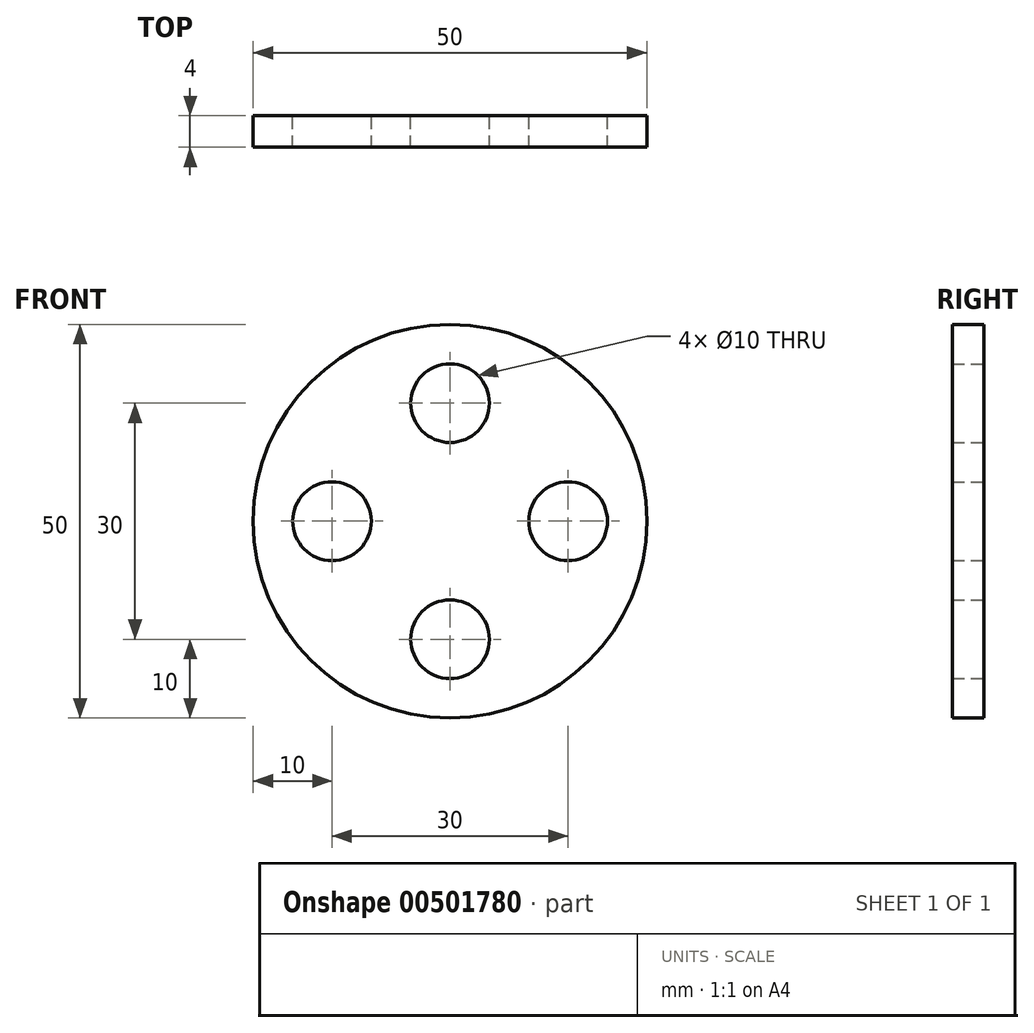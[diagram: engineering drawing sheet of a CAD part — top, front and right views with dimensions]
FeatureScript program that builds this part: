
annotation { "Feature Type Name" : "Feature", "Feature Type Description" : "" }
export const myFeature = defineFeature(function(context is Context, id is Id, definition is map)
    precondition{}
    {
        {
            var Q0;
            Q0=qCreatedBy(makeId("Front.planeOp"),FACE);
            var sketch = newSketch(context, id + "F0", { "sketchPlane" : qUnion([Q0])});
            skCircle(sketch, "E0", {"center": v(0, 0) * mm, "radius": 25 * mm});
            skCircle(sketch, "E1", {"center": v(0, 15) * mm, "radius": 5 * mm});
            skCircle(sketch, "E2.1.0", {"center": v(15, 0) * mm, "radius": 5 * mm});
            skCircle(sketch, "E2.2.0", {"center": v(0, -15) * mm, "radius": 5 * mm});
            skLineSegment(sketch, "E2.anchor1", {"start": v(0, 0) * mm, "end": v(0, 15) * mm, "construction": true});
            skLineSegment(sketch, "E2.anchor2", {"start": v(0, 0) * mm, "end": v(-15, 0) * mm, "construction": true});
            skCircle(sketch, "E3.1.3.0", {"center": v(-15, 0) * mm, "radius": 5 * mm});
            skSolve(sketch);
        }
        {
            var Q0;
            Q0=makeQuery(id+"F0.imprint","IMPRINT",FACE,{"disambiguationData":[TD([[makeQuery(id+"F0.imprint","IMPRINT",EDGE,{"derivedFrom":sQuery(id+"F0.wireOp",EDGE,"E0")}),1.0]])]});
            extrude(context, id + "F1", {"entities" : qUnion([Q0]), "depth" : 4 * mm});
        }
    });
